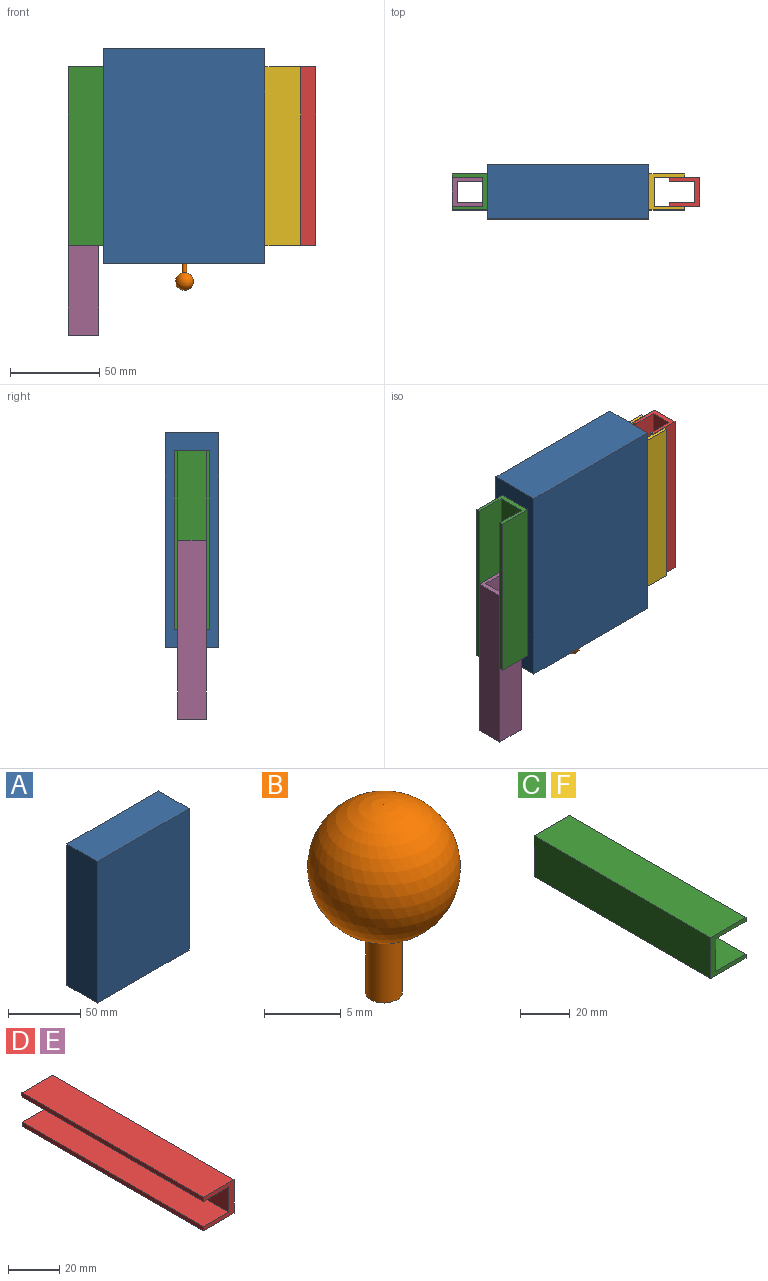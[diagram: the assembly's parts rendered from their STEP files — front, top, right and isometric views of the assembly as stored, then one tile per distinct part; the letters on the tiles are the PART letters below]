
ASSEMBLY  parts=6 mates=5
PART A: 12 faces, bbox 90x30x120 mm
  f0: plane 120x90mm, normal (0,1,0), area 1025mm2, adj f1,f2,f3,f4,f6,f7,f8,f9
  f1: plane 90x30mm, normal (0,0,-1), area 2692.5mm2, adj f0,f2,f4,f5,f11
  f2: plane 120x30mm, normal (1,0,0), area 3600mm2, adj f0,f1,f3,f5
  f3: plane 90x30mm, normal (0,0,1), area 2700mm2, adj f0,f2,f4,f5
  f4: plane 120x30mm, normal (-1,0,0), area 3600mm2, adj f0,f1,f3,f5
  f5: plane 120x90mm, normal (0,-1,0), area 10800mm2, adj f1,f2,f3,f4
  f6: plane 85x27.5mm, normal (0,0,1), area 2330mm2, adj f0,f7,f9,f10,f11
  f7: plane 115x27.5mm, normal (-1,0,0), area 3162.5mm2, adj f0,f6,f8,f10
  f8: plane 85x27.5mm, normal (0,0,-1), area 2337.5mm2, adj f0,f7,f9,f10
  f9: plane 115x27.5mm, normal (1,0,0), area 3162.5mm2, adj f0,f6,f8,f10
  f10: plane 115x85mm, normal (0,1,0), area 9775mm2, adj f6,f7,f8,f9
  f11: cylinder r=1.55mm len=3.1mm, axis (0,0,-1), area 24.3mm2, adj f1,f6
PART B: 3 faces, bbox 10x10x15 mm
  f0: plane 2.41x2.41mm, normal (0,0,-1), area 4.6mm2, adj f1
  f1: cylinder r=1.2mm len=5.15mm, axis (0,0,1), area 38.9mm2, adj f0,f2
  f2: sphere r=5mm, area 309.5mm2, adj f1
PART C: 10 faces, bbox 20x100x20 mm
  f0: plane 100x17mm, normal (0,0,-1), area 1700mm2, adj f1,f7,f8,f9
  f1: plane 100x2mm, normal (1,0,0), area 200mm2, adj f0,f2,f8,f9
  f2: plane 100x20mm, normal (0,0,1), area 2000mm2, adj f1,f3,f8,f9
  f3: plane 100x20mm, normal (-1,0,0), area 2000mm2, adj f2,f4,f8,f9
  f4: plane 100x20mm, normal (0,0,-1), area 2000mm2, adj f3,f5,f8,f9
  f5: plane 100x2mm, normal (1,0,0), area 200mm2, adj f4,f6,f8,f9
  f6: plane 100x17mm, normal (0,0,1), area 1700mm2, adj f5,f7,f8,f9
  f7: plane 100x16mm, normal (1,0,0), area 1600mm2, adj f0,f6,f8,f9
  f8: plane 20x20mm, normal (0,-1,0), area 128mm2, adj f0,f1,f2,f3,f4,f5,f6,f7
  f9: plane 20x20mm, normal (0,1,0), area 128mm2, adj f0,f1,f2,f3,f4,f5,f6,f7
PART D: 10 faces, bbox 17x100x16 mm
  f0: plane 100x2mm, normal (-1,0,0), area 200mm2, adj f1,f7,f8,f9
  f1: plane 100x14mm, normal (0,0,-1), area 1400mm2, adj f0,f2,f8,f9
  f2: plane 100x12mm, normal (-1,0,0), area 1200mm2, adj f1,f3,f8,f9
  f3: plane 100x14mm, normal (0,0,1), area 1400mm2, adj f2,f4,f8,f9
  f4: plane 100x2mm, normal (-1,0,0), area 200mm2, adj f3,f5,f8,f9
  f5: plane 100x17mm, normal (0,0,-1), area 1700mm2, adj f4,f6,f8,f9
  f6: plane 100x16mm, normal (1,0,0), area 1600mm2, adj f5,f7,f8,f9
  f7: plane 100x17mm, normal (0,0,1), area 1700mm2, adj f0,f6,f8,f9
  f8: plane 17x16mm, normal (0,-1,0), area 104mm2, adj f0,f1,f2,f3,f4,f5,f6,f7
  f9: plane 17x16mm, normal (0,1,0), area 104mm2, adj f0,f1,f2,f3,f4,f5,f6,f7
PART E: same geometry as D
PART F: same geometry as C
PLACE A t=(-54.93,-5.05,38.77)mm
PLACE B rot(axis=(1,0,0),180deg) t=(-54.93,-20.05,-31.23)mm
PLACE C rot(axis=(0,-0.71,0.71),180deg) t=(-119.93,-10.05,-11.23)mm
PLACE D rot(axis=(-1,0,0),90deg) t=(1.57,-28.05,-11.23)mm
PLACE E rot(axis=(0,-0.71,0.71),180deg) t=(-102.93,-12.05,-61.23)mm
PLACE F rot(axis=(1,0,0),90deg) t=(10.07,-10.05,88.77)mm
MATE fastened B.f1 <-> A.f11  axis (0,0,1) through (-54.93,-20.05,-21.23)mm
MATE planar E.f7 <-> C.f0  axis (0,-1,0) through (-111.43,-28.05,-11.23)mm
MATE fastened F.f3 <-> A.f2  axis (-1,0,0) through (-9.93,-20.05,38.77)mm
MATE fastened C.f3 <-> A.f4  axis (1,0,0) through (-99.93,-20.05,38.77)mm
MATE planar D.f5 <-> F.f0  axis (0,-1,0) through (1.57,-28.05,38.77)mm
